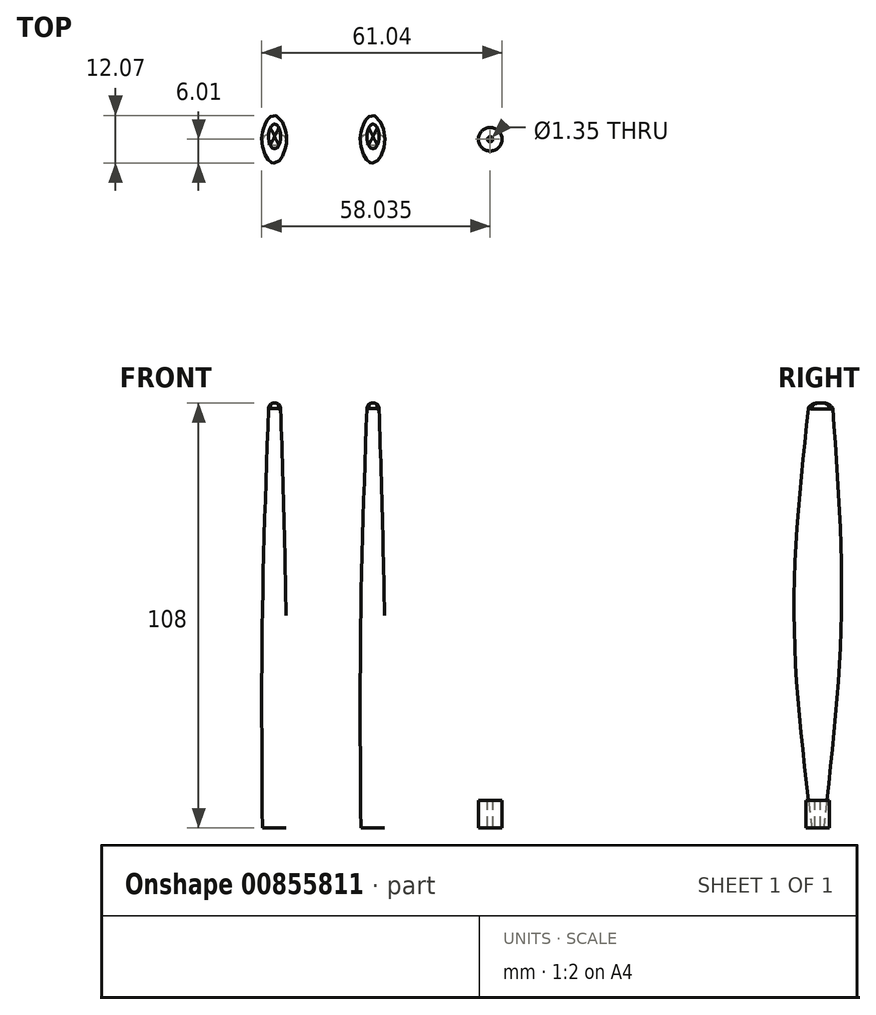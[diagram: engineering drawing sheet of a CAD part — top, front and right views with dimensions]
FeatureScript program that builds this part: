
annotation { "Feature Type Name" : "Feature", "Feature Type Description" : "" }
export const myFeature = defineFeature(function(context is Context, id is Id, definition is map)
    precondition{}
    {
        {
            var Q0;
            Q0=qCreatedBy(makeId("Top.planeOp"),FACE);
            var sketch = newSketch(context, id + "F0", { "sketchPlane" : qUnion([Q0])});
            skEllipse(sketch, "E0", {"center": v(0, 0) * mm, "majorRadius": 3 * mm, "minorRadius": 1.5 * mm, "majorAxis": v(1, 0)});
            skSolve(sketch);
        }
        {
            var Q0;
            Q0=qCreatedBy(makeId("Top.planeOp"),FACE);
            cPlane(context, id + "F1", {"entities" : qUnion([Q0]), "cplaneType" : CPlaneType.OFFSET, "offset" : 54 * mm, "width" : 150 * mm, "height" : 150 * mm});
        }
        {
            var Q0;
            Q0=qCreatedBy(id+"F1.planeOp",FACE);
            var sketch = newSketch(context, id + "F2", { "sketchPlane" : qUnion([Q0])});
            skEllipse(sketch, "E1", {"center": v(0, 0) * mm, "majorRadius": 3 * mm, "minorRadius": 6 * mm, "majorAxis": v(1, 0)});
            skSolve(sketch);
        }
        {
            var Q0;
            Q0=qCreatedBy(id+"F1.planeOp",FACE);
            cPlane(context, id + "F3", {"entities" : qUnion([Q0]), "cplaneType" : CPlaneType.OFFSET, "offset" : 54 * mm, "width" : 150 * mm, "height" : 150 * mm});
        }
        {
            var Q0;
            Q0=qCreatedBy(id+"F3.planeOp",FACE);
            var sketch = newSketch(context, id + "F4", { "sketchPlane" : qUnion([Q0])});
            skEllipse(sketch, "E2", {"center": v(0.1, 0.74) * mm, "majorRadius": 1.5 * mm, "minorRadius": 3 * mm, "majorAxis": v(1, 0)});
            skSolve(sketch);
        }
        {
            var Q0;
            Q0=makeQuery(id+"F0.imprint","IMPRINT",FACE,{"disambiguationData":[TD([[makeQuery(id+"F0.imprint","IMPRINT",EDGE,{"derivedFrom":sQuery(id+"F0.wireOp",EDGE,"E0")}),1.0]])]});
            var Q1;
            Q1=makeQuery(id+"F2.imprint","IMPRINT",FACE,{"disambiguationData":[TD([[makeQuery(id+"F2.imprint","IMPRINT",EDGE,{"derivedFrom":sQuery(id+"F2.wireOp",EDGE,"E1")}),1.0]])]});
            var Q2;
            Q2=makeQuery(id+"F4.imprint","IMPRINT",FACE,{"disambiguationData":[TD([[makeQuery(id+"F4.imprint","IMPRINT",EDGE,{"derivedFrom":sQuery(id+"F4.wireOp",EDGE,"E2")}),1.0]])]});
            loft(context, id + "F5", {"sheetProfilesArray" : [{ "sheetProfileEntities" : qUnion([Q0]) }, { "sheetProfileEntities" : qUnion([Q1]) }, { "sheetProfileEntities" : qUnion([Q2]) }]});
        }
        {
            var Q0;
            Q0=makeQuery(id+"F5.opLoft","SWEPT_BODY",BODY,{"disambiguationData":[OSD([makeQuery(id+"F0.imprint","IMPRINT",FACE,{"disambiguationData":[TD([[makeQuery(id+"F0.imprint","IMPRINT",EDGE,{"derivedFrom":sQuery(id+"F0.wireOp",EDGE,"E0")}),1.0]])]}),sQuery(id+"F2.wireOp",EDGE,"E1"),makeQuery(id+"F4.imprint","IMPRINT",FACE,{"disambiguationData":[TD([[makeQuery(id+"F4.imprint","IMPRINT",EDGE,{"derivedFrom":sQuery(id+"F4.wireOp",EDGE,"E2")}),1.0]])]})])]});
            var Q1;
            Q1=makeQuery(id+"F5.opLoft","SWEPT_FACE",FACE,{"disambiguationData":[OSD([sQuery(id+"F0.wireOp",EDGE,"E0"),sQuery(id+"F2.wireOp",EDGE,"E1"),sQuery(id+"F4.wireOp",EDGE,"E2")])]});
            transform(context, id + "F6", {"entities" : qUnion([Q0]), "transformType" : TransformType.COPY});
        }
        {
            var Q0;
            Q0=makeQuery(id+"F6.opPattern","COPY",BODY,{"derivedFrom":makeQuery(id+"F5.opLoft","SWEPT_BODY",BODY,{"disambiguationData":[OSD([makeQuery(id+"F0.imprint","IMPRINT",FACE,{"disambiguationData":[TD([[makeQuery(id+"F0.imprint","IMPRINT",EDGE,{"derivedFrom":sQuery(id+"F0.wireOp",EDGE,"E0")}),1.0]])]}),sQuery(id+"F2.wireOp",EDGE,"E1"),makeQuery(id+"F4.imprint","IMPRINT",FACE,{"disambiguationData":[TD([[makeQuery(id+"F4.imprint","IMPRINT",EDGE,{"derivedFrom":sQuery(id+"F4.wireOp",EDGE,"E2")}),1.0]])]})])]}),"instanceName":"1"});
            var Q1;
            Q1=qCreatedBy(makeId("Right.planeOp"),FACE);
            transform(context, id + "F7", {"entities" : qUnion([Q0]), "transformType" : TransformType.TRANSLATION_DISTANCE, "transformDirection" : qUnion([Q1]), "distance" : 25 * mm, "makeCopy" : false});
        }
        {
            var Q0;
            Q0=qCreatedBy(makeId("Top.planeOp"),FACE);
            var sketch = newSketch(context, id + "F8", { "sketchPlane" : qUnion([Q0])});
            skEllipse(sketch, "E3", {"center": v(54.88, 0) * mm, "majorRadius": 3 * mm, "minorRadius": 3 * mm, "majorAxis": v(1, 0)});
            skSolve(sketch);
        }
        {
            var Q0;
            Q0=makeQuery(id+"F8.imprint","IMPRINT",FACE,{"disambiguationData":[TD([[makeQuery(id+"F8.imprint","IMPRINT",EDGE,{"derivedFrom":sQuery(id+"F8.wireOp",EDGE,"E3")}),1.0]])]});
            var Q1;
            Q1 = qConstructionFilter(qBodyType(qCreatedBy(id + "F8" ,EDGE), BodyType.WIRE), ConstructionObject.NO);
            extrude(context, id + "F9", {"entities" : qUnion([Q0]), "surfaceEntities" : qUnion([Q1]), "depth" : 7 * mm, "offsetDistance" : 25 * mm});
        }
        {
            var Q0;
            Q0=makeQuery(id+"F6.opPattern","COPY",EDGE,{"derivedFrom":makeQuery(id+"F5.opLoft","MID_CAP_EDGE",EDGE,{"disambiguationData":[OSD([sQuery(id+"F4.wireOp",EDGE,"E2")])],"capPos":2.0}),"instanceName":"1"});
            var Q1;
            Q1=makeQuery(id+"F5.opLoft","MID_CAP_EDGE",EDGE,{"disambiguationData":[OSD([sQuery(id+"F4.wireOp",EDGE,"E2")])],"capPos":2.0});
            fillet(context, id + "F10", {"entities" : qUnion([Q0, Q1]), "radius" : 1.55 * mm, "rho" : 0.5, "crossSection" : FilletCrossSection.CONIC, "allowEdgeOverflow" : false});
        }
        {
            var Q0;
            Q0=makeQuery(id+"F9.opExtrude","CAP_FACE",FACE,{"disambiguationData":[OSD([sQuery(id+"F8.wireOp",EDGE,"E3")])],"isStart":false});
            var sketch = newSketch(context, id + "F11", { "sketchPlane" : qUnion([Q0])});
            skCircle(sketch, "E4", {"center": v(54.88, 0) * mm, "radius": 0.68 * mm});
            skSolve(sketch);
        }
        {
            var Q0;
            Q0 = qSketchRegion(id + "F11", true);
            extrude(context, id + "F12", {"entities" : qUnion([Q0]), "operationType" : NewBodyOperationType.REMOVE, "oppositeDirection" : true, "depth" : 8 * mm, "offsetDistance" : 25 * mm});
        }
    });
